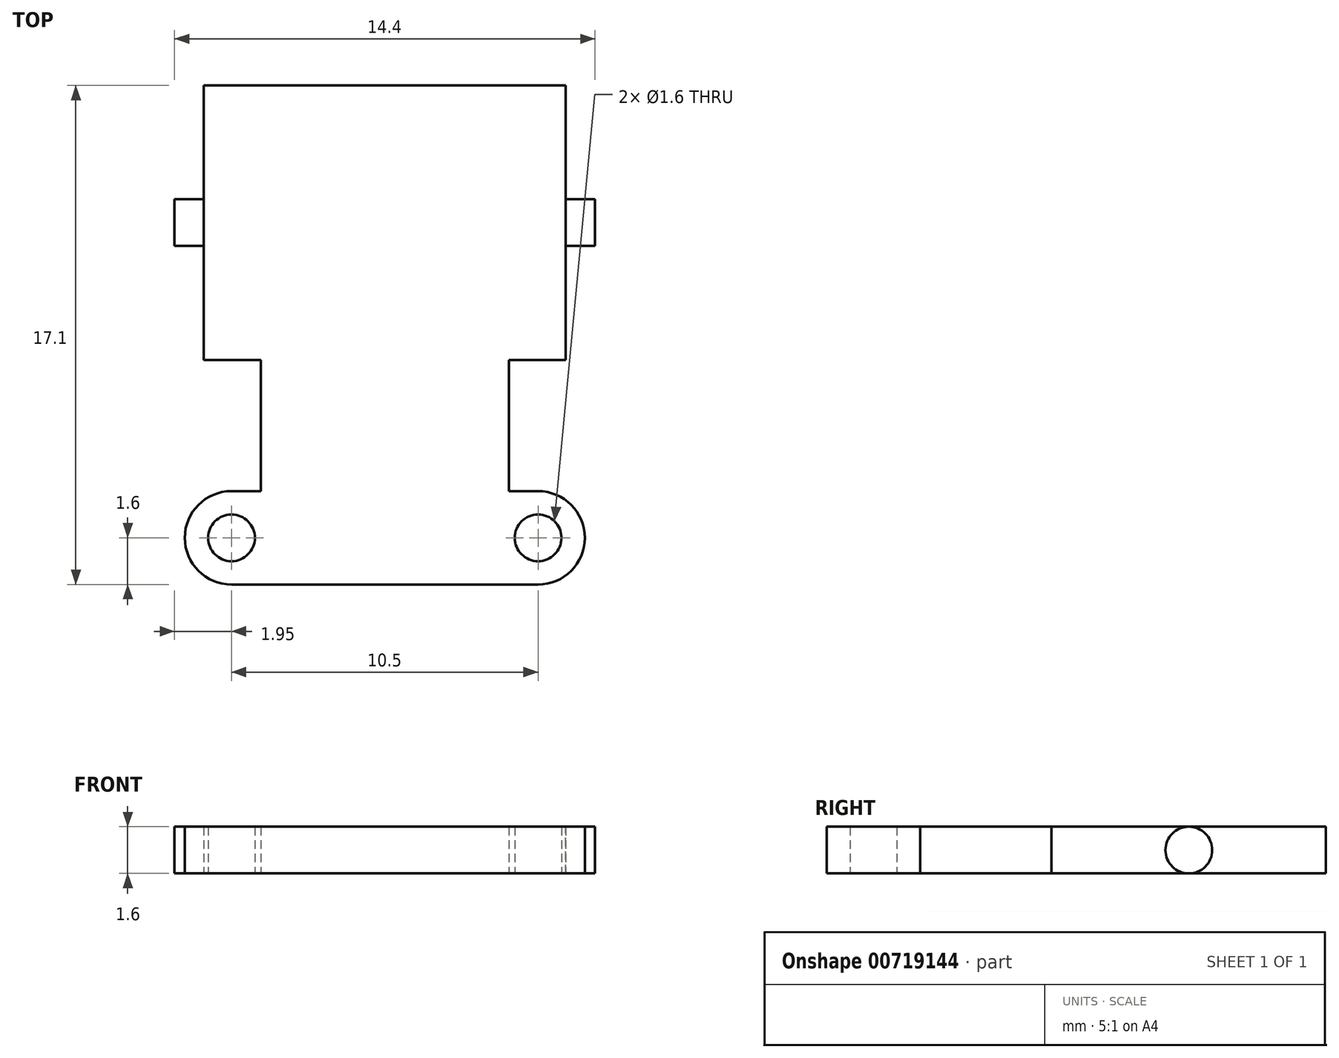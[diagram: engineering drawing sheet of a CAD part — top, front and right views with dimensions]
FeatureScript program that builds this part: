
annotation { "Feature Type Name" : "Feature", "Feature Type Description" : "" }
export const myFeature = defineFeature(function(context is Context, id is Id, definition is map)
    precondition{}
    {
        {
            var Q0;
            Q0=qCreatedBy(makeId("Top.planeOp"),FACE);
            var sketch = newSketch(context, id + "F0", { "sketchPlane" : qUnion([Q0])});
            skLineSegment(sketch, "E0.bottom", {"start": v(0, 0) * mm, "end": v(1.95, 0) * mm});
            skLineSegment(sketch, "E0.top", {"start": v(0, 9.4) * mm, "end": v(12.4, 9.4) * mm});
            skLineSegment(sketch, "E0.left", {"start": v(0, 0) * mm, "end": v(0, 3.9) * mm});
            skLineSegment(sketch, "E0.right", {"start": v(12.4, 0) * mm, "end": v(12.4, 3.9) * mm});
            skLineSegment(sketch, "E1", {"start": v(1.95, 0) * mm, "end": v(1.95, -4.5) * mm});
            skLineSegment(sketch, "E2", {"start": v(10.45, -4.5) * mm, "end": v(10.45, 0) * mm});
            skLineSegment(sketch, "E3.trimOffspring", {"start": v(10.45, 0) * mm, "end": v(12.4, 0) * mm});
            skLineSegment(sketch, "E4", {"start": v(6.2, 9.4) * mm, "end": v(6.2, 5.33) * mm, "construction": true});
            skLineSegment(sketch, "E5", {"start": v(0.95, -4.5) * mm, "end": v(1.95, -4.5) * mm});
            skLineSegment(sketch, "E6.trimOffspring", {"start": v(10.45, -4.5) * mm, "end": v(11.45, -4.5) * mm});
            skLineSegment(sketch, "E7", {"start": v(0.95, -7.7) * mm, "end": v(11.45, -7.7) * mm});
            skCircle(sketch, "E8", {"center": v(0.95, -6.1) * mm, "radius": 0.8 * mm});
            skLineSegment(sketch, "E9", {"start": v(0.95, -6.1) * mm, "end": v(4.08, -6.1) * mm, "construction": true});
            skCircle(sketch, "E10.MirrorC", {"center": v(11.45, -6.1) * mm, "radius": 0.8 * mm});
            skLineSegment(sketch, "E11", {"start": v(0, 5.5) * mm, "end": v(-1, 5.5) * mm});
            skLineSegment(sketch, "E12", {"start": v(-1, 5.5) * mm, "end": v(-1, 3.9) * mm});
            skLineSegment(sketch, "E13", {"start": v(-1, 3.9) * mm, "end": v(0, 3.9) * mm});
            skLineSegment(sketch, "E14", {"start": v(12.4, 5.5) * mm, "end": v(13.4, 5.5) * mm});
            skLineSegment(sketch, "E15", {"start": v(13.4, 5.5) * mm, "end": v(13.4, 3.9) * mm});
            skLineSegment(sketch, "E16", {"start": v(13.4, 3.9) * mm, "end": v(12.4, 3.9) * mm});
            skLineSegment(sketch, "E17.trimOffspring", {"start": v(0, 5.5) * mm, "end": v(0, 9.4) * mm});
            skLineSegment(sketch, "E18.trimOffspring", {"start": v(12.4, 5.5) * mm, "end": v(12.4, 9.4) * mm});
            skLineSegment(sketch, "E19", {"start": v(-1, 4.7) * mm, "end": v(2.65, 4.7) * mm, "construction": true});
            skArc(sketch, "E20", {"start": v(0.95, -4.5) * mm, "mid": v(-0.65, -6.1) * mm, "end": v(0.95, -7.7) * mm});
            skArc(sketch, "E21.MirrorCS", {"start": v(11.45, -4.5) * mm, "mid": v(13.05, -6.1) * mm, "end": v(11.45, -7.7) * mm});
            skSolve(sketch);
        }
        {
            var Q0;
            Q0=qSketchRegion(id+"F0",true);
            extrude(context, id + "F1", {"entities" : qUnion([Q0]), "depth" : 1.6 * mm, "offsetDistance" : 25 * mm});
        }
        {
            var Q0;
            Q0=makeQuery(id+"F1.opExtrude","SWEPT_FACE",FACE,{"disambiguationData":[OSD([sQuery(id+"F0.wireOp",EDGE,"E12")])]});
            var sketch = newSketch(context, id + "F2", { "sketchPlane" : qUnion([Q0])});
            skCircle(sketch, "E22", {"center": v(-4.7, 0.8) * mm, "radius": 0.8 * mm});
            skPoint(sketch, "E22.centerSnap0", {"position": v(-5.5, 0.8) * mm});
            skLineSegment(sketch, "E23.bottom", {"start": v(-6.22, 2.5) * mm, "end": v(-3.07, 2.5) * mm});
            skLineSegment(sketch, "E23.top", {"start": v(-6.22, -0.72) * mm, "end": v(-3.07, -0.72) * mm});
            skLineSegment(sketch, "E23.left", {"start": v(-6.22, 2.5) * mm, "end": v(-6.22, -0.72) * mm});
            skLineSegment(sketch, "E23.right", {"start": v(-3.07, 2.5) * mm, "end": v(-3.07, -0.72) * mm});
            skSolve(sketch);
        }
        {
            var Q0;
            Q0=qSketchRegion(id+"F2",true);
            var Q1;
            Q1=makeQuery(id+"F1.opExtrude","SWEPT_FACE",FACE,{"disambiguationData":[OSD([sQuery(id+"F0.wireOp",EDGE,"E0.left")])]});
            extrude(context, id + "F3", {"entities" : qUnion([Q0]), "operationType" : NewBodyOperationType.REMOVE, "endBound" : BoundingType.UP_TO_SURFACE, "oppositeDirection" : true, "depth" : 25 * mm, "endBoundEntityFace" : qUnion([Q1]), "offsetDistance" : 25 * mm});
        }
        {
            var Q0;
            Q0=makeQuery(id+"F1.opExtrude","SWEPT_FACE",FACE,{"disambiguationData":[OSD([sQuery(id+"F0.wireOp",EDGE,"E15")])]});
            var sketch = newSketch(context, id + "F4", { "sketchPlane" : qUnion([Q0])});
            skCircle(sketch, "E24", {"center": v(4.7, 0.8) * mm, "radius": 0.8 * mm});
            skPoint(sketch, "E24.centerSnap0", {"position": v(5.5, 0.8) * mm});
            skLineSegment(sketch, "E25.bottom", {"start": v(3.3, 2.22) * mm, "end": v(6.2, 2.22) * mm});
            skLineSegment(sketch, "E25.top", {"start": v(3.3, -0.74) * mm, "end": v(6.2, -0.74) * mm});
            skLineSegment(sketch, "E25.left", {"start": v(3.3, 2.22) * mm, "end": v(3.3, -0.74) * mm});
            skLineSegment(sketch, "E25.right", {"start": v(6.2, 2.22) * mm, "end": v(6.2, -0.74) * mm});
            skSolve(sketch);
        }
        {
            var Q0;
            Q0=qSketchRegion(id+"F4",true);
            var Q1;
            Q1=makeQuery(id+"F1.opExtrude","SWEPT_FACE",FACE,{"disambiguationData":[OSD([sQuery(id+"F0.wireOp",EDGE,"E18.trimOffspring")])]});
            extrude(context, id + "F5", {"entities" : qUnion([Q0]), "operationType" : NewBodyOperationType.REMOVE, "endBound" : BoundingType.UP_TO_SURFACE, "oppositeDirection" : true, "depth" : 25 * mm, "endBoundEntityFace" : qUnion([Q1]), "offsetDistance" : 25 * mm});
        }
    });
